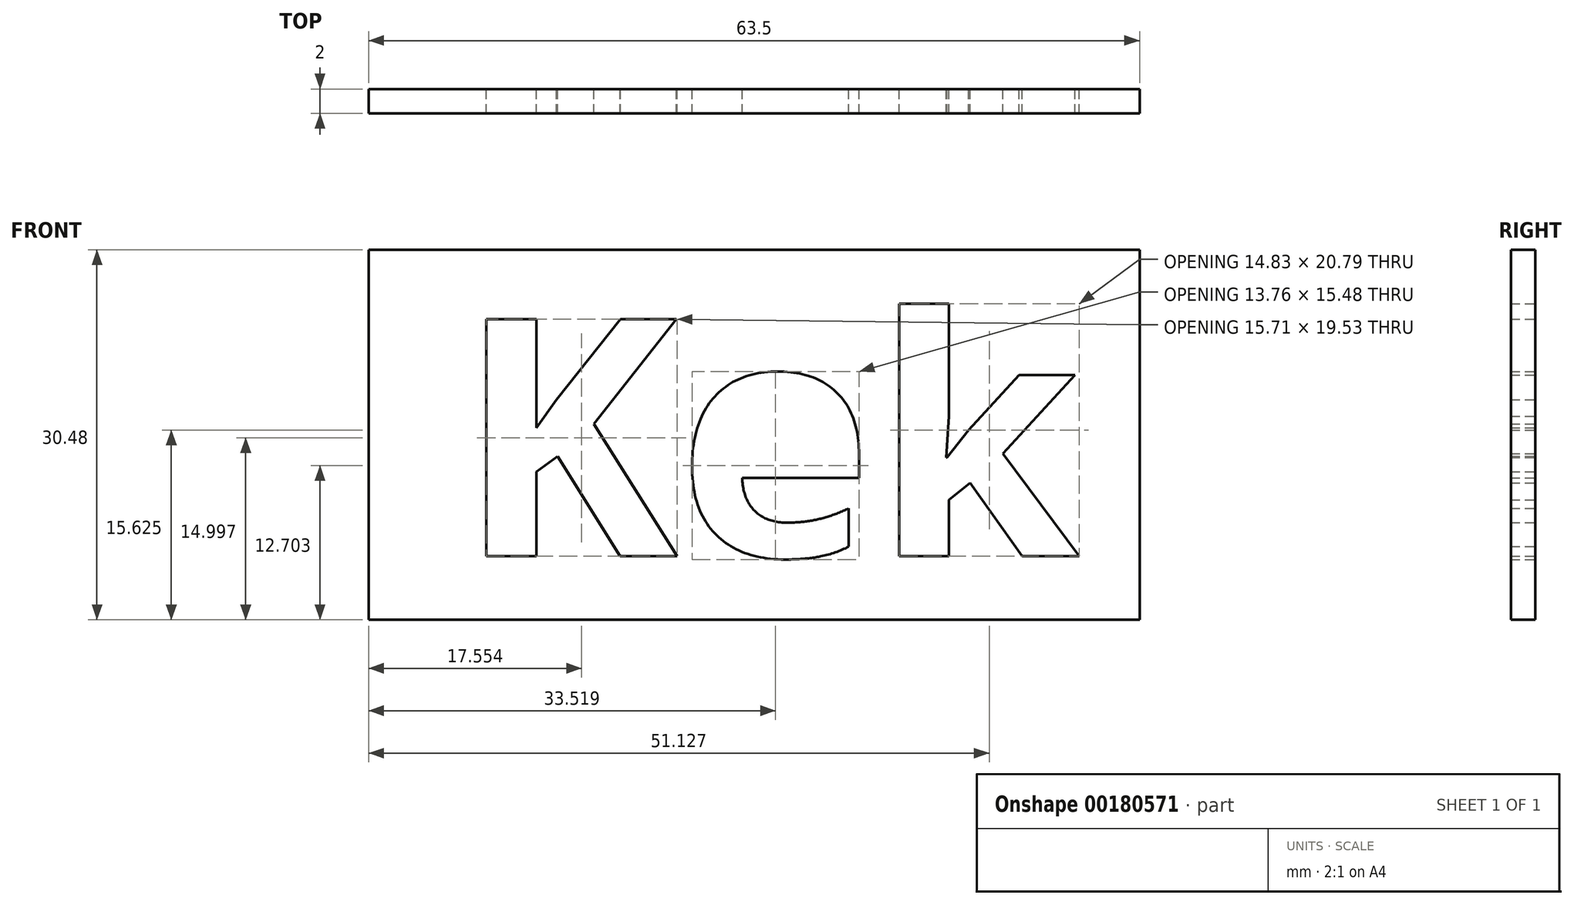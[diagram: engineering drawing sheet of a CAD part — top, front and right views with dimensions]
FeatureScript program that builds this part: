
annotation { "Feature Type Name" : "Feature", "Feature Type Description" : "" }
export const myFeature = defineFeature(function(context is Context, id is Id, definition is map)
    precondition{}
    {
        {
            var Q0;
            Q0=qCreatedBy(makeId("Front.planeOp"),FACE);
            var sketch = newSketch(context, id + "F0", { "sketchPlane" : qUnion([Q0])});
            skLineSegment(sketch, "E0.bottom", {"start": v(-40.78, 0) * mm, "end": v(22.72, 0) * mm});
            skLineSegment(sketch, "E0.top", {"start": v(-40.78, 30.48) * mm, "end": v(22.72, 30.48) * mm});
            skLineSegment(sketch, "E0.left", {"start": v(-40.78, 0) * mm, "end": v(-40.78, 30.48) * mm});
            skLineSegment(sketch, "E0.right", {"start": v(22.72, 0) * mm, "end": v(22.72, 30.48) * mm});
            skText(sketch, "E1", { "text": "Kek", "fontName": "OpenSans-Bold.ttf"});
            const initialGuessF0  = {"E1": [-0.03354, 0.00523, 1, 0, 0.0197]};
            skSetInitialGuess(sketch, initialGuessF0);
            skSolve(sketch);
        }
        {
            var Q0;
            Q0 = qSketchRegion(id + "F0", true);
            extrude(context, id + "F1", {"entities" : qUnion([Q0]), "depth" : 2 * mm});
        }
    });
